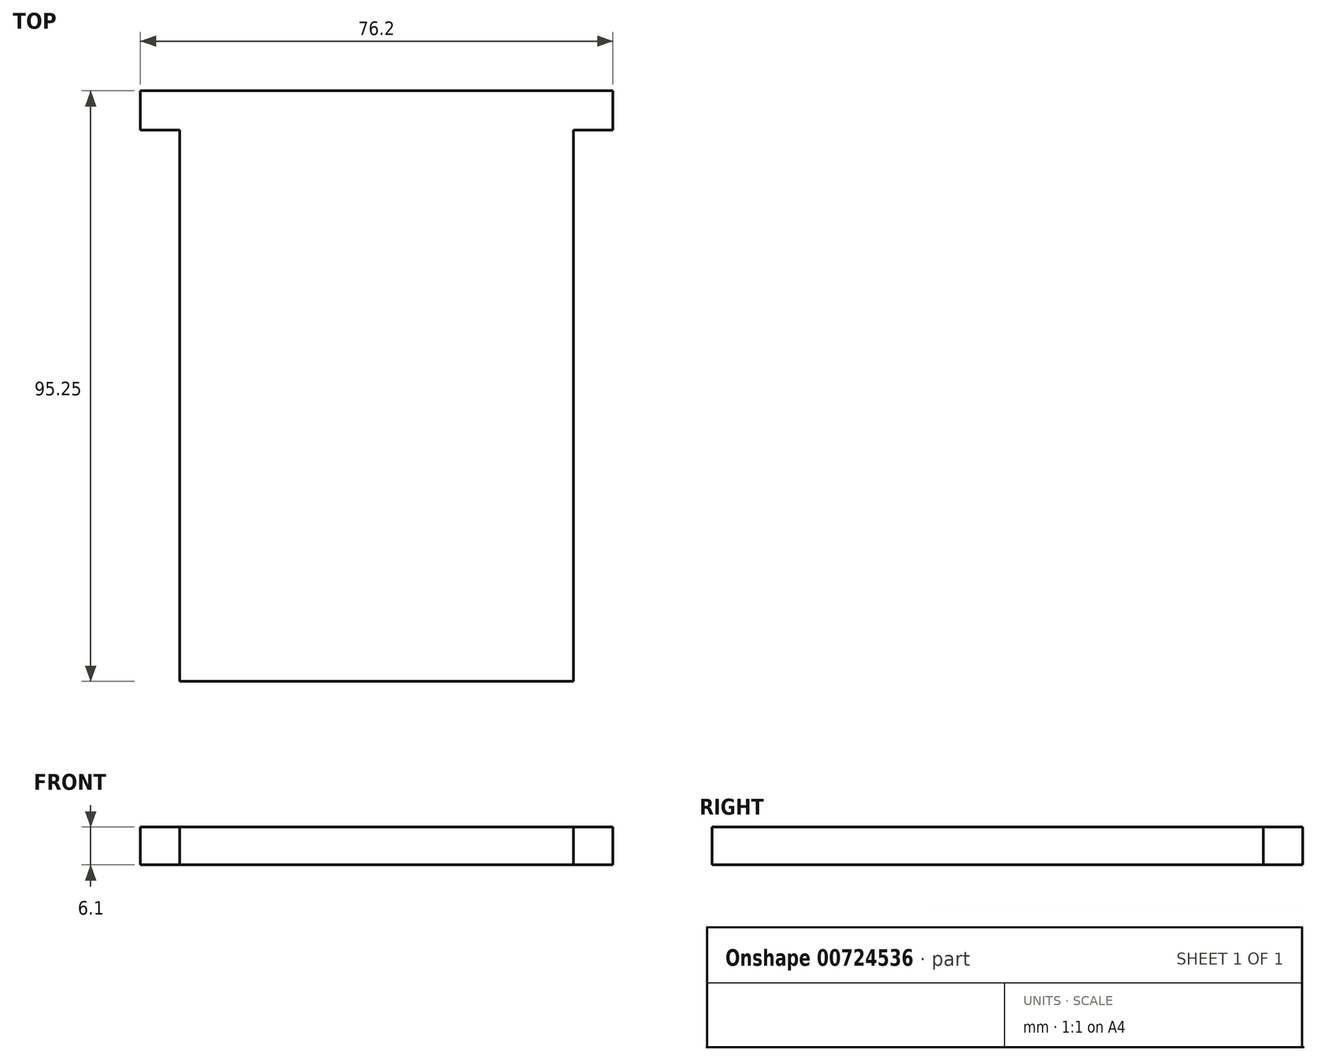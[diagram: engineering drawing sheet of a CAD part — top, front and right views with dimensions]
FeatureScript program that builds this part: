
annotation { "Feature Type Name" : "Feature", "Feature Type Description" : "" }
export const myFeature = defineFeature(function(context is Context, id is Id, definition is map)
    precondition{}
    {
        {
            var Q0;
            Q0=qCreatedBy(makeId("Top.planeOp"),FACE);
            var sketch = newSketch(context, id + "F0", { "sketchPlane" : qUnion([Q0])});
            skLineSegment(sketch, "E0", {"start": v(0, 0) * mm, "end": v(76.2, 0) * mm});
            skLineSegment(sketch, "E1", {"start": v(76.2, 0) * mm, "end": v(76.2, -6.35) * mm});
            skLineSegment(sketch, "E2", {"start": v(76.2, -6.35) * mm, "end": v(69.85, -6.35) * mm});
            skLineSegment(sketch, "E3", {"start": v(0, 0) * mm, "end": v(0, -6.35) * mm});
            skLineSegment(sketch, "E4", {"start": v(0, -6.35) * mm, "end": v(6.35, -6.35) * mm});
            skLineSegment(sketch, "E5", {"start": v(6.35, -6.35) * mm, "end": v(6.35, -95.25) * mm});
            skLineSegment(sketch, "E6", {"start": v(6.35, -95.25) * mm, "end": v(69.85, -95.25) * mm});
            skLineSegment(sketch, "E7", {"start": v(69.85, -95.25) * mm, "end": v(69.85, -6.35) * mm});
            skSolve(sketch);
        }
        {
            var Q0;
            Q0=makeQuery(id+"F0.imprint","IMPRINT",FACE,{"disambiguationData":[TD([[makeQuery(id+"F0.imprint","IMPRINT",EDGE,{"derivedFrom":sQuery(id+"F0.wireOp",EDGE,"E0")}),-1.0]])]});
            extrude(context, id + "F1", {"entities" : qUnion([Q0]), "depth" : 6.1 * mm, "offsetDistance" : 25.4 * mm});
        }
    });
